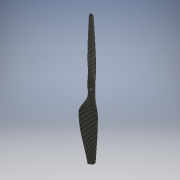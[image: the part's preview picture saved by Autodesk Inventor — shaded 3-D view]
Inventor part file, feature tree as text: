
AUTODESK INVENTOR PART (.ipt)
format: ipt  version: 2017 (Build 210142000, 142)  size: 370,688 bytes
history: native  units: mm
features: sketch x8, other x5, extrude x2, loft x1, pattern_circular x1
ambient origin geometry x8: Origin, YZ Plane, XZ Plane, XY Plane, X Axis, Y Axis, Z Axis, Center Point
bodies: Body1 (feature_tree)
feature tree (17):
  sketch  "Szkic1"
  other  "Płaszczyzna konstrukcyjna1"
  sketch  "Szkic2"
  other  "Płaszczyzna konstrukcyjna2"
  sketch  "Szkic3"
  other  "Płaszczyzna konstrukcyjna3"
  sketch  "Szkic4"
  other  "Płaszczyzna konstrukcyjna4"
  sketch  "Szkic5"
  other  "Płaszczyzna konstrukcyjna5"
  loft  "Wyciągnięcie złożone2"
  extrude  "Wyciągnięcie proste1"  Depth=12.0mm
  pattern_circular  "Szyk kołowy1"  [2 undecoded]
  extrude  "Wyciągnięcie proste2"  Depth=25.0mm
  sketch  "Szkic6"
  sketch  "Szkic7"
  sketch  "Szkic8"
note: 2 required parameter values undecoded (feature->parameter linkage not recoverable at this tier; creation-order binding heuristic only, values carry confidence <= 0.55)
